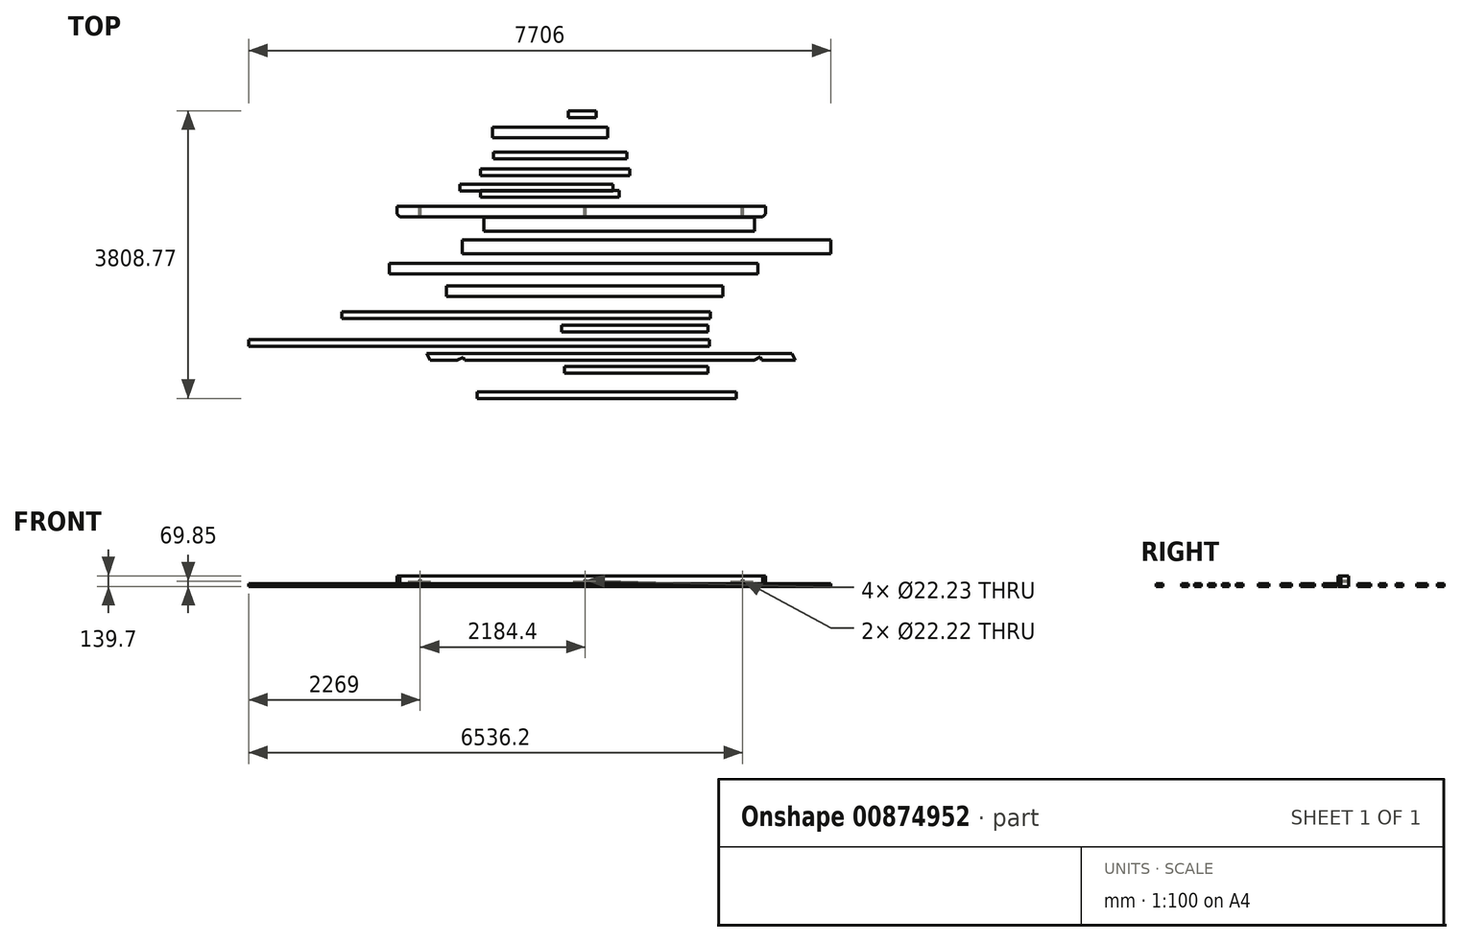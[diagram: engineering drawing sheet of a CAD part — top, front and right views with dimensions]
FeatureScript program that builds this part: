
annotation { "Feature Type Name" : "Feature", "Feature Type Description" : "" }
export const myFeature = defineFeature(function(context is Context, id is Id, definition is map)
    precondition{}
    {
        {
            var Q0;
            Q0=qCreatedBy(makeId("Top.planeOp"),FACE);
            var sketch = newSketch(context, id + "F0", { "sketchPlane" : qUnion([Q0])});
            skLineSegment(sketch, "E0.bottom", {"start": v(-1077.96, 99.24) * mm, "end": v(3798.84, 99.24) * mm});
            skLineSegment(sketch, "E0.top", {"start": v(-1077.96, -84.9) * mm, "end": v(3798.84, -84.9) * mm});
            skLineSegment(sketch, "E0.left", {"start": v(-1077.96, 99.24) * mm, "end": v(-1077.96, -84.9) * mm});
            skLineSegment(sketch, "E0.right", {"start": v(3798.84, 99.24) * mm, "end": v(3798.84, -84.9) * mm});
            skSolve(sketch);
        }
        {
            var Q0;
            Q0 = qSketchRegion(id + "F0", true);
            extrude(context, id + "F1", {"entities" : qUnion([Q0]), "depth" : 38.1 * mm, "offsetDistance" : 25.4 * mm});
        }
        {
            var Q0;
            Q0=qCreatedBy(makeId("Top.planeOp"),FACE);
            var sketch = newSketch(context, id + "F2", { "sketchPlane" : qUnion([Q0])});
            skLineSegment(sketch, "E1.bottom", {"start": v(-792.57, 397.91) * mm, "end": v(2788.83, 397.91) * mm});
            skLineSegment(sketch, "E1.top", {"start": v(-792.57, 213.76) * mm, "end": v(2788.83, 213.76) * mm});
            skLineSegment(sketch, "E1.left", {"start": v(-792.57, 397.91) * mm, "end": v(-792.57, 213.76) * mm});
            skLineSegment(sketch, "E1.right", {"start": v(2788.83, 397.91) * mm, "end": v(2788.83, 213.76) * mm});
            skSolve(sketch);
        }
        {
            var Q0;
            Q0=makeQuery(id+"F2.imprint","IMPRINT",FACE,{"disambiguationData":[TD([[makeQuery(id+"F2.imprint","IMPRINT",EDGE,{"derivedFrom":sQuery(id+"F2.wireOp",EDGE,"E1.bottom")}),-1.0]])]});
            extrude(context, id + "F3", {"entities" : qUnion([Q0]), "depth" : 38.1 * mm, "offsetDistance" : 25.4 * mm});
        }
        {
            var Q0;
            Q0=qCreatedBy(makeId("Top.planeOp"),FACE);
            var sketch = newSketch(context, id + "F4", { "sketchPlane" : qUnion([Q0])});
            skLineSegment(sketch, "E2.bottom", {"start": v(-1942.96, 546.46) * mm, "end": v(2933.84, 546.46) * mm});
            skLineSegment(sketch, "E2.top", {"start": v(-1942.96, 406.76) * mm, "end": v(2933.84, 406.76) * mm});
            skLineSegment(sketch, "E2.left", {"start": v(-1942.96, 546.46) * mm, "end": v(-1942.96, 406.76) * mm});
            skLineSegment(sketch, "E2.right", {"start": v(2933.84, 546.46) * mm, "end": v(2933.84, 406.76) * mm});
            skSolve(sketch);
        }
        {
            var Q0;
            Q0=makeQuery(id+"F4.imprint","IMPRINT",FACE,{"disambiguationData":[TD([[makeQuery(id+"F4.imprint","IMPRINT",EDGE,{"derivedFrom":sQuery(id+"F4.wireOp",EDGE,"E2.bottom")}),-1.0]])]});
            extrude(context, id + "F5", {"entities" : qUnion([Q0]), "depth" : 139.7 * mm, "offsetDistance" : 25.4 * mm});
        }
        {
            var Q0;
            Q0=makeQuery(id+"F5.opExtrude","SWEPT_EDGE",EDGE,{"disambiguationData":[OSD([sQuery(id+"F4.wireOp",EDGE,"E2.top"),sQuery(id+"F4.wireOp",EDGE,"E2.left")])]});
            var Q1;
            Q1=makeQuery(id+"F5.opExtrude","SWEPT_EDGE",EDGE,{"disambiguationData":[OSD([sQuery(id+"F4.wireOp",EDGE,"E2.top"),sQuery(id+"F4.wireOp",EDGE,"E2.right")])]});
            chamfer(context, id + "F6", {"entities" : qUnion([Q0, Q1]), "width" : 38.1 * mm, "tangentPropagation" : true});
        }
        {
            var Q0;
            Q0=qCreatedBy(makeId("Top.planeOp"),FACE);
            var sketch = newSketch(context, id + "F7", { "sketchPlane" : qUnion([Q0])});
            skLineSegment(sketch, "E3.bottom", {"start": v(-2043.5, -207.9) * mm, "end": v(2833.3, -207.9) * mm});
            skLineSegment(sketch, "E3.top", {"start": v(-2043.5, -347.6) * mm, "end": v(2833.3, -347.6) * mm});
            skLineSegment(sketch, "E3.left", {"start": v(-2043.5, -207.9) * mm, "end": v(-2043.5, -347.6) * mm});
            skLineSegment(sketch, "E3.right", {"start": v(2833.3, -207.9) * mm, "end": v(2833.3, -347.6) * mm});
            skSolve(sketch);
        }
        {
            var Q0;
            Q0=makeQuery(id+"F7.imprint","IMPRINT",FACE,{"disambiguationData":[TD([[makeQuery(id+"F7.imprint","IMPRINT",EDGE,{"derivedFrom":sQuery(id+"F7.wireOp",EDGE,"E3.bottom")}),-1.0]])]});
            extrude(context, id + "F8", {"entities" : qUnion([Q0]), "depth" : 38.1 * mm, "offsetDistance" : 25.4 * mm});
        }
        {
            var Q0;
            Q0=qCreatedBy(makeId("Top.planeOp"),FACE);
            var sketch = newSketch(context, id + "F9", { "sketchPlane" : qUnion([Q0])});
            skLineSegment(sketch, "E4.bottom", {"start": v(-1286.89, -507.8) * mm, "end": v(2370.71, -507.8) * mm});
            skLineSegment(sketch, "E4.top", {"start": v(-1286.89, -647.5) * mm, "end": v(2370.71, -647.5) * mm});
            skLineSegment(sketch, "E4.left", {"start": v(-1286.89, -507.8) * mm, "end": v(-1286.89, -647.5) * mm});
            skLineSegment(sketch, "E4.right", {"start": v(2370.71, -507.8) * mm, "end": v(2370.71, -647.5) * mm});
            skSolve(sketch);
        }
        {
            var Q0;
            Q0 = qSketchRegion(id + "F9", true);
            extrude(context, id + "F10", {"entities" : qUnion([Q0]), "depth" : 38.1 * mm, "offsetDistance" : 25.4 * mm});
        }
        {
            var Q0;
            Q0=qCreatedBy(makeId("Top.planeOp"),FACE);
            var sketch = newSketch(context, id + "F11", { "sketchPlane" : qUnion([Q0])});
            skLineSegment(sketch, "E5.bottom", {"start": v(235.54, -1030.57) * mm, "end": v(2172.29, -1030.57) * mm});
            skLineSegment(sketch, "E5.top", {"start": v(235.54, -1119.47) * mm, "end": v(2172.29, -1119.47) * mm});
            skLineSegment(sketch, "E5.left", {"start": v(235.54, -1030.57) * mm, "end": v(235.54, -1119.47) * mm});
            skLineSegment(sketch, "E5.right", {"start": v(2172.29, -1030.57) * mm, "end": v(2172.29, -1119.47) * mm});
            skSolve(sketch);
        }
        {
            var Q0;
            Q0 = qSketchRegion(id + "F11", true);
            extrude(context, id + "F12", {"entities" : qUnion([Q0]), "depth" : 38.1 * mm, "offsetDistance" : 25.4 * mm});
        }
        {
            var Q0;
            Q0=qCreatedBy(makeId("Top.planeOp"),FACE);
            var sketch = newSketch(context, id + "F13", { "sketchPlane" : qUnion([Q0])});
            skLineSegment(sketch, "E6.bottom", {"start": v(-2674.9, -849.92) * mm, "end": v(2201.9, -849.92) * mm});
            skLineSegment(sketch, "E6.top", {"start": v(-2674.9, -938.82) * mm, "end": v(2201.9, -938.82) * mm});
            skLineSegment(sketch, "E6.left", {"start": v(-2674.9, -849.92) * mm, "end": v(-2674.9, -938.82) * mm});
            skLineSegment(sketch, "E6.right", {"start": v(2201.9, -849.92) * mm, "end": v(2201.9, -938.82) * mm});
            skSolve(sketch);
        }
        {
            var Q0;
            Q0 = qSketchRegion(id + "F13", true);
            extrude(context, id + "F14", {"entities" : qUnion([Q0]), "depth" : 38.1 * mm, "offsetDistance" : 25.4 * mm});
        }
        {
            var Q0;
            Q0=qCreatedBy(makeId("Top.planeOp"),FACE);
            var sketch = newSketch(context, id + "F15", { "sketchPlane" : qUnion([Q0])});
            skLineSegment(sketch, "E7.bottom", {"start": v(-3907.16, -1215.46) * mm, "end": v(2188.84, -1215.46) * mm});
            skLineSegment(sketch, "E7.top", {"start": v(-3907.16, -1304.36) * mm, "end": v(2188.84, -1304.36) * mm});
            skLineSegment(sketch, "E7.left", {"start": v(-3907.16, -1215.46) * mm, "end": v(-3907.16, -1304.36) * mm});
            skLineSegment(sketch, "E7.right", {"start": v(2188.84, -1215.46) * mm, "end": v(2188.84, -1304.36) * mm});
            skSolve(sketch);
        }
        {
            var Q0;
            Q0 = qSketchRegion(id + "F15", true);
            extrude(context, id + "F16", {"entities" : qUnion([Q0]), "depth" : 38.1 * mm, "offsetDistance" : 25.4 * mm});
        }
        {
            var Q0;
            Q0=qCreatedBy(makeId("Top.planeOp"),FACE);
            var sketch = newSketch(context, id + "F17", { "sketchPlane" : qUnion([Q0])});
            skLineSegment(sketch, "E8.bottom", {"start": v(-1547.27, -1402.12) * mm, "end": v(3285.07, -1402.12) * mm});
            skLineSegment(sketch, "E8.top", {"start": v(-1502.81, -1491.02) * mm, "end": v(-1147.8, -1491.02) * mm});
            skLineSegment(sketch, "E9", {"start": v(-1547.27, -1402.12) * mm, "end": v(-1502.81, -1491.02) * mm});
            skLineSegment(sketch, "E10", {"start": v(3329.53, -1491.02) * mm, "end": v(3285.07, -1402.12) * mm});
            skLineSegment(sketch, "E11", {"start": v(-1068.3, -1451.27) * mm, "end": v(-1048.42, -1491.02) * mm});
            skLineSegment(sketch, "E12", {"start": v(-1068.3, -1451.27) * mm, "end": v(-1147.8, -1491.02) * mm});
            skLineSegment(sketch, "E13.trimOffspring", {"start": v(-1048.42, -1491.02) * mm, "end": v(2779.83, -1491.02) * mm});
            skLineSegment(sketch, "E14", {"start": v(2884.88, -1491.02) * mm, "end": v(2863.86, -1449) * mm});
            skLineSegment(sketch, "E15", {"start": v(2863.86, -1449) * mm, "end": v(2779.83, -1491.02) * mm});
            skLineSegment(sketch, "E16.trimOffspring", {"start": v(2884.88, -1491.02) * mm, "end": v(3329.53, -1491.02) * mm});
            skSolve(sketch);
        }
        {
            var Q0;
            Q0 = qSketchRegion(id + "F17", true);
            extrude(context, id + "F18", {"entities" : qUnion([Q0]), "depth" : 38.1 * mm, "offsetDistance" : 25.4 * mm});
        }
        {
            var Q0;
            Q0=qCreatedBy(makeId("Top.planeOp"),FACE);
            var sketch = newSketch(context, id + "F19", { "sketchPlane" : qUnion([Q0])});
            skLineSegment(sketch, "E17.bottom", {"start": v(-882.36, -1907.7) * mm, "end": v(2546.64, -1907.7) * mm});
            skLineSegment(sketch, "E17.top", {"start": v(-882.36, -1996.6) * mm, "end": v(2546.64, -1996.6) * mm});
            skLineSegment(sketch, "E17.left", {"start": v(-882.36, -1907.7) * mm, "end": v(-882.36, -1996.6) * mm});
            skLineSegment(sketch, "E17.right", {"start": v(2546.64, -1907.7) * mm, "end": v(2546.64, -1996.6) * mm});
            skSolve(sketch);
        }
        {
            var Q0;
            Q0=makeQuery(id+"F19.imprint","IMPRINT",FACE,{"disambiguationData":[TD([[makeQuery(id+"F19.imprint","IMPRINT",EDGE,{"derivedFrom":sQuery(id+"F19.wireOp",EDGE,"E17.bottom")}),-1.0]])]});
            extrude(context, id + "F20", {"entities" : qUnion([Q0]), "depth" : 38.1 * mm, "offsetDistance" : 25.4 * mm});
        }
        {
            var Q0;
            Q0=qCreatedBy(makeId("Top.planeOp"),FACE);
            var sketch = newSketch(context, id + "F21", { "sketchPlane" : qUnion([Q0])});
            skLineSegment(sketch, "E18.bottom", {"start": v(274.38, -1571.96) * mm, "end": v(2173.03, -1571.96) * mm});
            skLineSegment(sketch, "E18.top", {"start": v(274.38, -1660.86) * mm, "end": v(2173.03, -1660.86) * mm});
            skLineSegment(sketch, "E18.left", {"start": v(274.38, -1571.96) * mm, "end": v(274.38, -1660.86) * mm});
            skLineSegment(sketch, "E18.right", {"start": v(2173.03, -1571.96) * mm, "end": v(2173.03, -1660.86) * mm});
            skSolve(sketch);
        }
        {
            var Q0;
            Q0 = qSketchRegion(id + "F21", true);
            extrude(context, id + "F22", {"entities" : qUnion([Q0]), "depth" : 38.1 * mm, "offsetDistance" : 25.4 * mm});
        }
        {
            var Q0;
            Q0=qCreatedBy(makeId("Top.planeOp"),FACE);
            var sketch = newSketch(context, id + "F23", { "sketchPlane" : qUnion([Q0])});
            skLineSegment(sketch, "E19.bottom", {"start": v(-1108.88, 839.2) * mm, "end": v(910.42, 839.2) * mm});
            skLineSegment(sketch, "E19.top", {"start": v(-1108.88, 750.3) * mm, "end": v(910.42, 750.3) * mm});
            skLineSegment(sketch, "E19.left", {"start": v(-1108.88, 839.2) * mm, "end": v(-1108.88, 750.3) * mm});
            skLineSegment(sketch, "E19.right", {"start": v(910.42, 839.2) * mm, "end": v(910.42, 750.3) * mm});
            skSolve(sketch);
        }
        {
            var Q0;
            Q0=makeQuery(id+"F23.imprint","IMPRINT",FACE,{"disambiguationData":[TD([[makeQuery(id+"F23.imprint","IMPRINT",EDGE,{"derivedFrom":sQuery(id+"F23.wireOp",EDGE,"E19.bottom")}),-1.0]])]});
            extrude(context, id + "F24", {"entities" : qUnion([Q0]), "depth" : 38.1 * mm, "offsetDistance" : 25.4 * mm});
        }
        {
            var Q0;
            Q0=qCreatedBy(makeId("Top.planeOp"),FACE);
            var sketch = newSketch(context, id + "F25", { "sketchPlane" : qUnion([Q0])});
            skLineSegment(sketch, "E20.bottom", {"start": v(-839.92, 1044.68) * mm, "end": v(1134.93, 1044.68) * mm});
            skLineSegment(sketch, "E20.top", {"start": v(-839.92, 955.78) * mm, "end": v(1134.93, 955.78) * mm});
            skLineSegment(sketch, "E20.left", {"start": v(-839.92, 1044.68) * mm, "end": v(-839.92, 955.78) * mm});
            skLineSegment(sketch, "E20.right", {"start": v(1134.93, 1044.68) * mm, "end": v(1134.93, 955.78) * mm});
            skLineSegment(sketch, "E21.bottom", {"start": v(-664.9, 1263.62) * mm, "end": v(1100.4, 1263.62) * mm});
            skLineSegment(sketch, "E21.top", {"start": v(-664.9, 1174.72) * mm, "end": v(1100.4, 1174.72) * mm});
            skLineSegment(sketch, "E21.left", {"start": v(-664.9, 1263.62) * mm, "end": v(-664.9, 1174.72) * mm});
            skLineSegment(sketch, "E21.right", {"start": v(1100.4, 1263.62) * mm, "end": v(1100.4, 1174.72) * mm});
            skLineSegment(sketch, "E22.bottom", {"start": v(-680.21, 1592.31) * mm, "end": v(843.79, 1592.31) * mm});
            skLineSegment(sketch, "E22.top", {"start": v(-680.21, 1452.61) * mm, "end": v(843.79, 1452.61) * mm});
            skLineSegment(sketch, "E22.left", {"start": v(-680.21, 1592.31) * mm, "end": v(-680.21, 1452.61) * mm});
            skLineSegment(sketch, "E22.right", {"start": v(843.79, 1592.31) * mm, "end": v(843.79, 1452.61) * mm});
            skLineSegment(sketch, "E23.bottom", {"start": v(-839.92, 758.8) * mm, "end": v(995.23, 758.8) * mm});
            skLineSegment(sketch, "E23.top", {"start": v(-839.92, 669.9) * mm, "end": v(995.23, 669.9) * mm});
            skLineSegment(sketch, "E23.left", {"start": v(-839.92, 758.8) * mm, "end": v(-839.92, 669.9) * mm});
            skLineSegment(sketch, "E23.right", {"start": v(995.23, 758.8) * mm, "end": v(995.23, 669.9) * mm});
            skLineSegment(sketch, "E24.bottom", {"start": v(324.69, 1812.16) * mm, "end": v(692.99, 1812.16) * mm});
            skLineSegment(sketch, "E24.top", {"start": v(324.69, 1723.26) * mm, "end": v(692.99, 1723.26) * mm});
            skLineSegment(sketch, "E24.left", {"start": v(324.69, 1812.16) * mm, "end": v(324.69, 1723.26) * mm});
            skLineSegment(sketch, "E24.right", {"start": v(692.99, 1812.16) * mm, "end": v(692.99, 1723.26) * mm});
            skSolve(sketch);
        }
        {
            var Q0;
            Q0 = qSketchRegion(id + "F25", true);
            extrude(context, id + "F26", {"entities" : qUnion([Q0]), "depth" : 38.1 * mm, "offsetDistance" : 25.4 * mm});
        }
        {
            var Q0;
            Q0=makeQuery(id+"F5.opExtrude","SWEPT_FACE",FACE,{"disambiguationData":[OSD([sQuery(id+"F4.wireOp",EDGE,"E2.bottom")])]});
            var sketch = newSketch(context, id + "F27", { "sketchPlane" : qUnion([Q0])});
            skCircle(sketch, "E25", {"center": v(-2629.04, 69.85) * mm, "radius": 11.11 * mm});
            skCircle(sketch, "E26", {"center": v(1638.16, 69.85) * mm, "radius": 11.11 * mm});
            skCircle(sketch, "E27", {"center": v(-546.24, 69.85) * mm, "radius": 11.11 * mm});
            skSolve(sketch);
        }
        {
            var Q0;
            Q0 = qSketchRegion(id + "F27", true);
            extrude(context, id + "F28", {"entities" : qUnion([Q0]), "operationType" : NewBodyOperationType.REMOVE, "endBound" : BoundingType.THROUGH_ALL, "oppositeDirection" : true, "depth" : 25.4 * mm, "offsetDistance" : 25.4 * mm});
        }
    });
